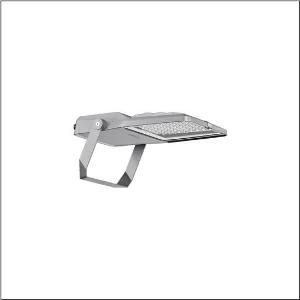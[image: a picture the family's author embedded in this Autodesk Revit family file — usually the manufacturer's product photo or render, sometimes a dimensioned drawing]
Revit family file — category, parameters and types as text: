
# Revit family: floodlight_fl_21_mini___pl52_5xa7775d2d1a_5239
name_source: partatom
category: Lighting Fixtures
units: mm (PartAtom-declared; Revit-internal decimal feet)

## family parameters
Cut with Voids When Loaded = No
Host = Face
Light Source = No
Part Type = Normal
Room Calculation Point = No
Round Connector Dimension = Use Diameter
Shared = No

## types (1)
- --- (1 x LED, 17840 lm, 142.9 W, 3000K)
    Apparent Load = 143 VA
    CIE Flux Codes = 26 60 98 100 100
    Color Rendering = 70
    Color Temperature = 3000K
    Default Elevation = 1800 mm
    Description = Floodlight FL 21 mini, floodlight, primary light control with lens, of PMMA, primary optical cover: protective disc, of toughened safety glass, transparent, light distribution: PL52, light emission: direct distribution, installation type: surface-mounted, LED, High Power LED, rated luminous flux: 17.840lm, luminous efficacy: 125lm/W, light colour: 730, colour temperature: 3000K, control: flexible luminous flux parameterisation, time-dependent luminous flux control, constant luminous flux control, overheat protection, presetting dimming logarithmic, with terminal, 6-pole, mains connection: 220..240V, AC, 50/60Hz, start of lifetime: 143W, end of service life: 151W, reduction: 63W, luminaire housing, of diecast aluminium, powder-coated, Siteco® metallic grey (DB 702S), corrosivity category C5 mid according to DIN EN ISO 12944, sealing non-destructively replaceable, mounting bracket, of steel, galvanised, powder-coated, Siteco® metallic grey (DB 702S), Smart Interface above, protection rating (complete): IP66, insulation class (complete): insulation class II (safety insulation), certification: CE, ENEC, VDE, protection symbol: D, impact resistance: IK08, permissible operating ambient temperature: -40..+40°C, permissible operating ambient temperature for outdoor applications: -40..+50°C, standard: DIN EN 12944, LABS conformity tested according to VDMA 24364:2018-05, packaging unit: 1 piece

Light Distribution: PL52
    Height = 70 mm
    Lamp = 1 x LED
    Lamp Light Flux = 17840 lm
    Lamp Power = 142.9 W
    Lamp count = 1
    Length = 485 mm
    Luminous efficacy = 125 lm/W
    Manufacturer = Siteco
    ModVariant = No
    Model = 5XA7775D2D1A
    Number of Poles = 1
    OnlyDefault = Yes
    Power Factor = 1
    Product Name = Floodlight FL 21 mini | PL52
    Product group = floodlight | pylon annexe
    ProductGroupID = 6200
    Protection Class = Protection class II
    Protection Degree = IP 66
    RLX_Detail_Level = 1
    RLX_Emergency_Light_Flux = 0 lm
    RLX_Emergency_Type = 0
    RLX_Emergency_Type_DB = No
    RlxData = <blob elided: 96385 chars, md5=4b092b37>
    Socket = socket
    Standby Power = 0 W
    System Light Flux = 17840 lm
    System Power = 143 W
    Type Comments = factory setting: luminous flux: 100 % | dim-lin: 254 | 730 mA
    Type Image = l_1006845.jpg
    URL = http://relux.com
    VarID = @adj_095521
    Voltage = 0 V
    Weight = 0.00 kg
    Width = 337 mm

## geometry (parser evidence)
native form markers: Blend x4, Sweep x12
no freeform markers — native parametric forms only
